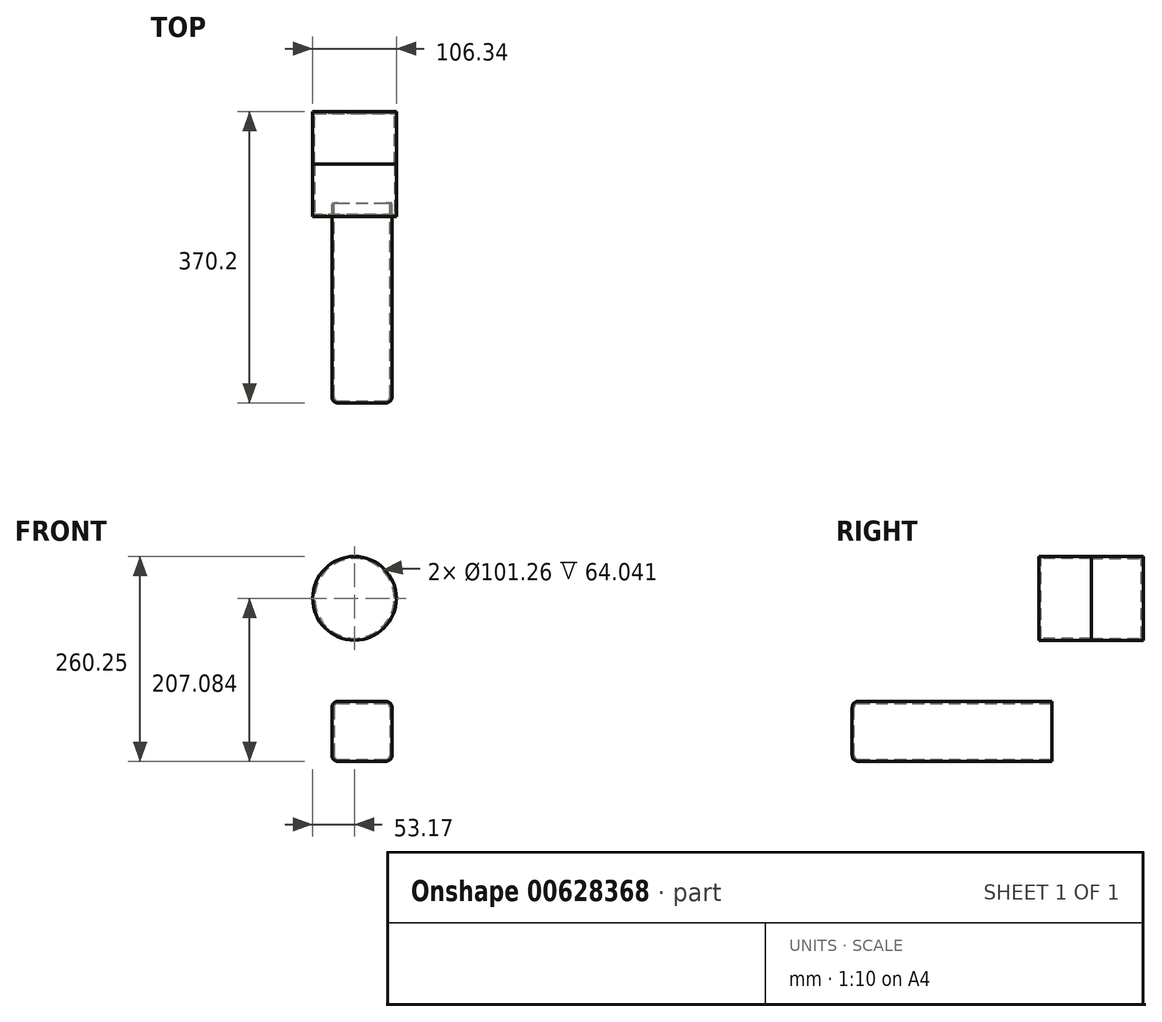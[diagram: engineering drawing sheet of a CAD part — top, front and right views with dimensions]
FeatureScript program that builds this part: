
annotation { "Feature Type Name" : "Feature", "Feature Type Description" : "" }
export const myFeature = defineFeature(function(context is Context, id is Id, definition is map)
    precondition{}
    {
        {
            var Q0;
            Q0=qCreatedBy(makeId("Front.planeOp"),FACE);
            var sketch = newSketch(context, id + "F0", { "sketchPlane" : qUnion([Q0])});
            skLineSegment(sketch, "E0.bottom", {"start": v(-28.63, 0) * mm, "end": v(47.57, 0) * mm});
            skLineSegment(sketch, "E0.top", {"start": v(-28.63, -76.2) * mm, "end": v(47.57, -76.2) * mm});
            skLineSegment(sketch, "E0.left", {"start": v(-28.63, 0) * mm, "end": v(-28.63, -76.2) * mm});
            skLineSegment(sketch, "E0.right", {"start": v(47.57, 0) * mm, "end": v(47.57, -76.2) * mm});
            skSolve(sketch);
        }
        {
            var Q0;
            Q0=makeQuery(id+"F0.imprint","IMPRINT",FACE,{"disambiguationData":[TD([[makeQuery(id+"F0.imprint","IMPRINT",EDGE,{"derivedFrom":sQuery(id+"F0.wireOp",EDGE,"E0.bottom")}),-1.0]])]});
            extrude(context, id + "F1", {"entities" : qUnion([Q0]), "depth" : 254 * mm, "offsetDistance" : 25.4 * mm});
        }
        {
            var Q0;
            Q0=makeQuery(id+"F1.opExtrude","CAP_FACE",FACE,{"disambiguationData":[OSD([sQuery(id+"F0.wireOp",EDGE,"E0.bottom"),sQuery(id+"F0.wireOp",EDGE,"E0.top"),sQuery(id+"F0.wireOp",EDGE,"E0.left"),sQuery(id+"F0.wireOp",EDGE,"E0.right")])],"isStart":false});
            var Q1;
            Q1=makeQuery(id+"F1.opExtrude","SWEPT_EDGE",EDGE,{"disambiguationData":[OSD([sQuery(id+"F0.wireOp",EDGE,"E0.top"),sQuery(id+"F0.wireOp",EDGE,"E0.left")])]});
            var Q2;
            Q2=makeQuery(id+"F1.opExtrude","SWEPT_EDGE",EDGE,{"disambiguationData":[OSD([sQuery(id+"F0.wireOp",EDGE,"E0.bottom"),sQuery(id+"F0.wireOp",EDGE,"E0.left")])]});
            var Q3;
            Q3=makeQuery(id+"F1.opExtrude","SWEPT_EDGE",EDGE,{"disambiguationData":[OSD([sQuery(id+"F0.wireOp",EDGE,"E0.top"),sQuery(id+"F0.wireOp",EDGE,"E0.right")])]});
            var Q4;
            Q4=makeQuery(id+"F1.opExtrude","SWEPT_EDGE",EDGE,{"disambiguationData":[OSD([sQuery(id+"F0.wireOp",EDGE,"E0.bottom"),sQuery(id+"F0.wireOp",EDGE,"E0.right")])]});
            fillet(context, id + "F2", {"entities" : qUnion([Q0, Q1, Q2, Q3, Q4]), "radius" : 7.62 * mm, "tangentPropagation" : true, "allowEdgeOverflow" : false});
        }
        {
            var Q0;
            Q0=makeQuery(id+"F1.opExtrude","CAP_FACE",FACE,{"disambiguationData":[OSD([sQuery(id+"F0.wireOp",EDGE,"E0.bottom"),sQuery(id+"F0.wireOp",EDGE,"E0.top"),sQuery(id+"F0.wireOp",EDGE,"E0.left"),sQuery(id+"F0.wireOp",EDGE,"E0.right")])],"isStart":true});
            shell(context, id + "F3", {"entities" : qUnion([Q0]), "thickness" : 2.54 * mm});
        }
        {
            var Q0;
            Q0=qCreatedBy(makeId("Right.planeOp"),FACE);
            var sketch = newSketch(context, id + "F4", { "sketchPlane" : qUnion([Q0])});
            skLineSegment(sketch, "E1.bottom", {"start": v(-16.96, 130.88) * mm, "end": v(49.62, 130.88) * mm});
            skLineSegment(sketch, "E1.top", {"start": v(-16.96, 77.72) * mm, "end": v(49.62, 77.72) * mm});
            skLineSegment(sketch, "E1.left", {"start": v(-16.96, 130.88) * mm, "end": v(-16.96, 77.72) * mm});
            skLineSegment(sketch, "E1.right", {"start": v(49.62, 130.88) * mm, "end": v(49.62, 77.72) * mm});
            skSolve(sketch);
        }
        {
            var Q0;
            Q0=makeQuery(id+"F4.imprint","IMPRINT",FACE,{"disambiguationData":[TD([[makeQuery(id+"F4.imprint","IMPRINT",EDGE,{"derivedFrom":sQuery(id+"F4.wireOp",EDGE,"E1.bottom")}),-1.0]])]});
            var Q1;
            Q1=sQuery(id+"F4.wireOp",EDGE,"E1.bottom");
            revolve(context, id + "F5", {"operationType" : NewBodyOperationType.ADD, "entities" : qUnion([Q0]), "axis" : qUnion([Q1]), "revolveType" : RevolveType.FULL});
        }
        {
            var Q0;
            Q0=makeQuery(id+"F5.opRevolve","SWEPT_FACE",FACE,{"disambiguationData":[OSD([sQuery(id+"F4.wireOp",EDGE,"E1.right")])]});
            shell(context, id + "F6", {"entities" : qUnion([Q0]), "thickness" : 2.54 * mm});
        }
        {
            var Q0;
            Q0=makeQuery(id+"F5.opRevolve","SWEPT_BODY",BODY,{"disambiguationData":[OSD([sQuery(id+"F4.wireOp",EDGE,"E1.bottom"),sQuery(id+"F4.wireOp",EDGE,"E1.top"),sQuery(id+"F4.wireOp",EDGE,"E1.left"),sQuery(id+"F4.wireOp",EDGE,"E1.right")])]});
            var Q1;
            Q1=makeQuery(id+"F5.opRevolve","SWEPT_FACE",FACE,{"disambiguationData":[OSD([sQuery(id+"F4.wireOp",EDGE,"E1.right")])]});
            mirror(context, id + "F7", {"operationType" : NewBodyOperationType.ADD, "entities" : qUnion([Q0]), "mirrorPlane" : qUnion([Q1])});
        }
    });
